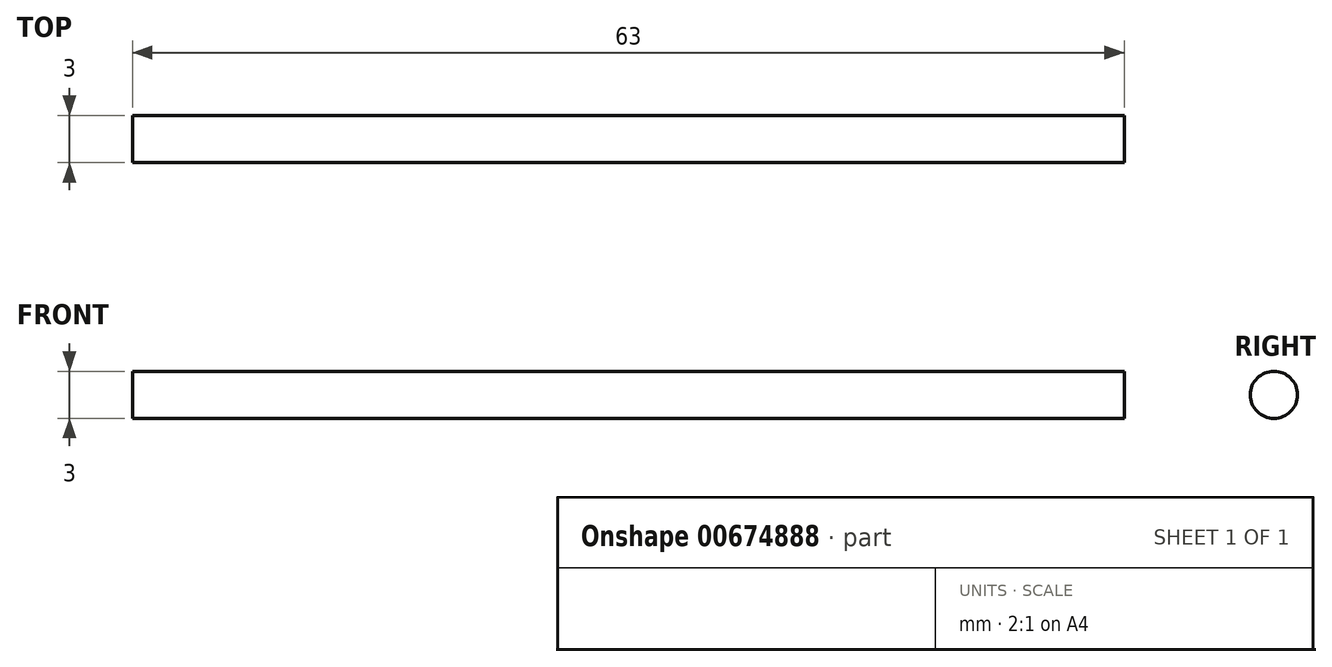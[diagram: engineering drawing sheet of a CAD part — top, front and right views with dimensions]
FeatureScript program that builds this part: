
annotation { "Feature Type Name" : "Feature", "Feature Type Description" : "" }
export const myFeature = defineFeature(function(context is Context, id is Id, definition is map)
    precondition{}
    {
        {
            var Q0;
            Q0=qCreatedBy(makeId("Right.planeOp"),FACE);
            var sketch = newSketch(context, id + "F0", { "sketchPlane" : qUnion([Q0])});
            skCircle(sketch, "E0", {"center": v(0, 0) * mm, "radius": 1.5 * mm});
            skSolve(sketch);
        }
        {
            var Q0;
            Q0=makeQuery(id+"F0.imprint","IMPRINT",FACE,{"disambiguationData":[TD([[makeQuery(id+"F0.imprint","IMPRINT",EDGE,{"derivedFrom":sQuery(id+"F0.wireOp",EDGE,"E0")}),1.0]])]});
            extrude(context, id + "F1", {"entities" : qUnion([Q0]), "depth" : 63 * mm, "offsetDistance" : 25.4 * mm});
        }
    });
